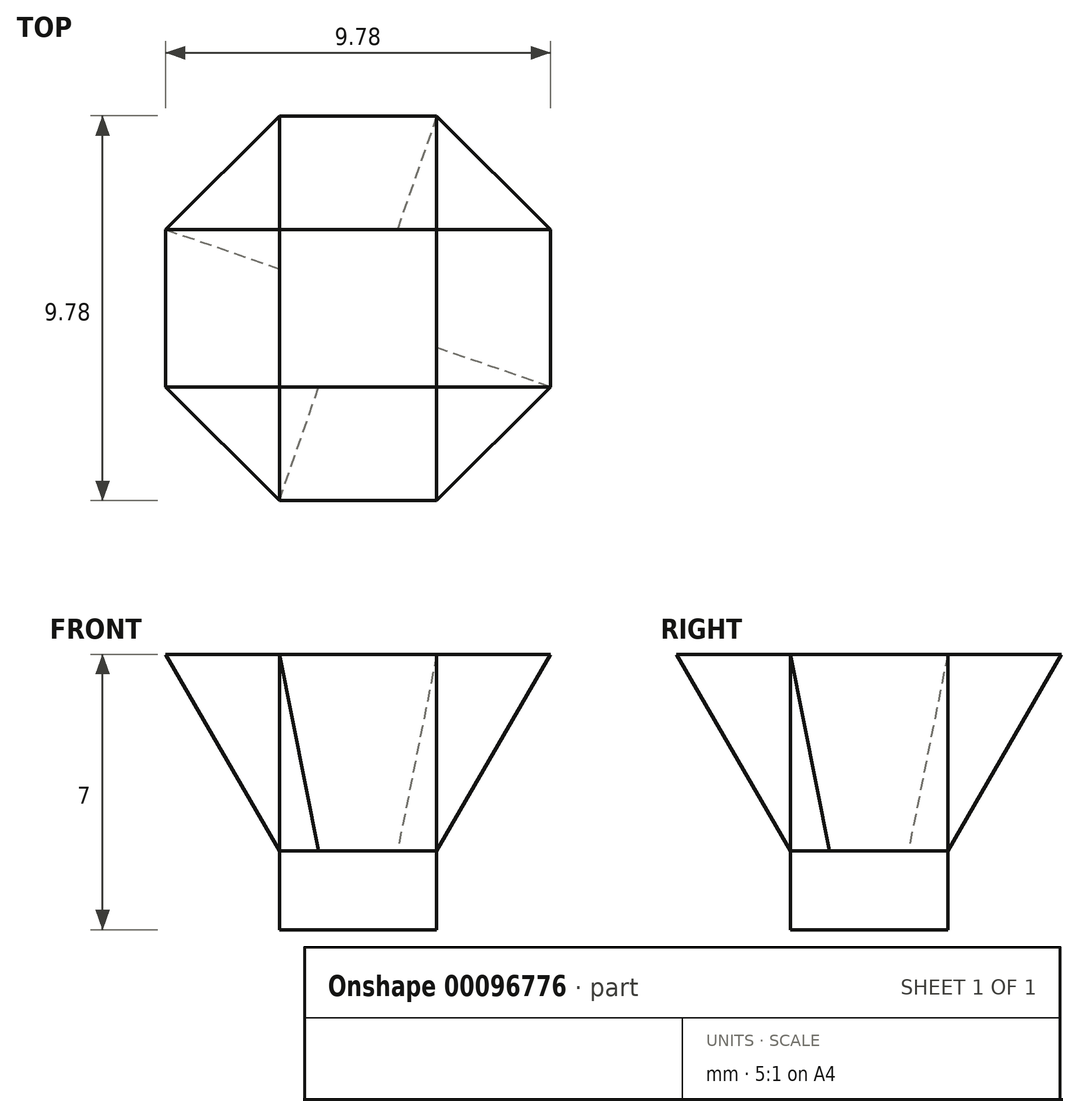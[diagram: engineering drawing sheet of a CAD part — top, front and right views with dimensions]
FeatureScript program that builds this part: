
annotation { "Feature Type Name" : "Feature", "Feature Type Description" : "" }
export const myFeature = defineFeature(function(context is Context, id is Id, definition is map)
    precondition{}
    {
        {
            var Q0;
            Q0=qCreatedBy(makeId("Front.planeOp"),FACE);
            var sketch = newSketch(context, id + "F0", { "sketchPlane" : qUnion([Q0])});
            skLineSegment(sketch, "E0.bottom", {"start": v(-2, 2.5) * mm, "end": v(2, 2.5) * mm});
            skLineSegment(sketch, "E0.top", {"start": v(-2, -2.5) * mm, "end": v(2, -2.5) * mm});
            skPoint(sketch, "E0.middle", {"position": v(0, 0) * mm});
            skLineSegment(sketch, "E1", {"start": v(-2, -2.5) * mm, "end": v(-4.89, 2.5) * mm});
            skLineSegment(sketch, "E2", {"start": v(0, 0) * mm, "end": v(0, 15.74) * mm, "construction": true});
            skLineSegment(sketch, "E3.MirrorCS", {"start": v(2, -2.5) * mm, "end": v(4.89, 2.5) * mm});
            skLineSegment(sketch, "E4", {"start": v(-2, 2.5) * mm, "end": v(-4.89, 2.5) * mm});
            skLineSegment(sketch, "E5", {"start": v(2, 2.5) * mm, "end": v(4.89, 2.5) * mm});
            skSolve(sketch);
        }
        {
            var Q0;
            Q0=qCreatedBy(makeId("Top.planeOp"),FACE);
            var sketch = newSketch(context, id + "F1", { "sketchPlane" : qUnion([Q0])});
            skPoint(sketch, "E6.0", {"position": v(-2, 0) * mm});
            skPoint(sketch, "E7.0", {"position": v(2, 0) * mm});
            skLineSegment(sketch, "E8.bottom", {"start": v(-2, -2) * mm, "end": v(2, -2) * mm});
            skLineSegment(sketch, "E8.top", {"start": v(-2, 2) * mm, "end": v(2, 2) * mm});
            skLineSegment(sketch, "E8.left", {"start": v(-2, -2) * mm, "end": v(-2, 2) * mm});
            skLineSegment(sketch, "E8.right", {"start": v(2, -2) * mm, "end": v(2, 2) * mm});
            skPoint(sketch, "E8.middle", {"position": v(0, 0) * mm});
            skSolve(sketch);
        }
        {
            var Q0;
            Q0=qCreatedBy(makeId("Top.planeOp"),FACE);
            cPlane(context, id + "F2", {"entities" : qUnion([Q0]), "cplaneType" : CPlaneType.OFFSET, "offset" : 2.5 * mm, "oppositeDirection" : true, "width" : 150 * mm, "height" : 150 * mm});
        }
        {
            var Q0;
            Q0=qCreatedBy(id+"F2.planeOp",FACE);
            var sketch = newSketch(context, id + "F3", { "sketchPlane" : qUnion([Q0])});
            skLineSegment(sketch, "E9.0.0", {"start": v(-2, 2) * mm, "end": v(-2, -2) * mm});
            skLineSegment(sketch, "E9.0.1", {"start": v(-2, -2) * mm, "end": v(2, -2) * mm});
            skLineSegment(sketch, "E9.0.2", {"start": v(2, -2) * mm, "end": v(2, 2) * mm});
            skLineSegment(sketch, "E9.0.3", {"start": v(2, 2) * mm, "end": v(-2, 2) * mm});
            skPoint(sketch, "E10", {"position": v(0, -2) * mm});
            skPoint(sketch, "E11", {"position": v(-2, 0) * mm});
            skPoint(sketch, "E12", {"position": v(0, 2) * mm});
            skPoint(sketch, "E13", {"position": v(2, 0) * mm});
            skLineSegment(sketch, "E14", {"start": v(-2, -2) * mm, "end": v(2, 2) * mm, "construction": true});
            skLineSegment(sketch, "E15", {"start": v(-2, 2) * mm, "end": v(2, -2) * mm, "construction": true});
            skLineSegment(sketch, "E16", {"start": v(0, -2) * mm, "end": v(0, 2) * mm, "construction": true});
            skLineSegment(sketch, "E17", {"start": v(-2, 0) * mm, "end": v(2, 0) * mm, "construction": true});
            skSolve(sketch);
        }
        {
            var Q0;
            Q0 = qSketchRegion(id + "F3", true);
            extrude(context, id + "F4", {"entities" : qUnion([Q0]), "oppositeDirection" : true, "depth" : 2 * mm});
        }
        {
            var Q0;
            Q0 = qSketchRegion(id + "F0", true);
            extrude(context, id + "F5", {"entities" : qUnion([Q0]), "operationType" : NewBodyOperationType.ADD, "depth" : 2 * mm, "hasSecondDirection" : true, "secondDirectionOppositeDirection" : true, "secondDirectionDepth" : 2 * mm});
        }
        {
            var Q0;
            Q0=qCreatedBy(makeId("Right.planeOp"),FACE);
            var sketch = newSketch(context, id + "F6", { "sketchPlane" : qUnion([Q0])});
            skLineSegment(sketch, "E18", {"start": v(0, -2.5) * mm, "end": v(2, -2.5) * mm});
            skLineSegment(sketch, "E19", {"start": v(0, -2.5) * mm, "end": v(-2, -2.5) * mm});
            skPoint(sketch, "E20.0", {"position": v(0, 2.5) * mm});
            skLineSegment(sketch, "E21", {"start": v(4.89, 2.5) * mm, "end": v(-4.89, 2.5) * mm});
            skLineSegment(sketch, "E22", {"start": v(2, -2.5) * mm, "end": v(4.89, 2.5) * mm});
            skLineSegment(sketch, "E23.MirrorCS", {"start": v(-2, -2.5) * mm, "end": v(-4.89, 2.5) * mm});
            skSolve(sketch);
        }
        {
            var Q0;
            Q0 = qSketchRegion(id + "F6", true);
            extrude(context, id + "F7", {"entities" : qUnion([Q0]), "depth" : 2 * mm, "hasSecondDirection" : true, "secondDirectionOppositeDirection" : true, "secondDirectionDepth" : 2 * mm});
        }
        {
            var Q0;
            Q0=qCreatedBy(makeId("Top.planeOp"),FACE);
            cPlane(context, id + "F8", {"entities" : qUnion([Q0]), "cplaneType" : CPlaneType.OFFSET, "offset" : 2.5 * mm, "width" : 150 * mm, "height" : 150 * mm});
        }
        {
            var Q0;
            Q0=qCreatedBy(id+"F8.planeOp",FACE);
            var sketch = newSketch(context, id + "F9", { "sketchPlane" : qUnion([Q0])});
            skLineSegment(sketch, "E24.0", {"start": v(2, 4.89) * mm, "end": v(-2, 4.89) * mm});
            skLineSegment(sketch, "E25.0", {"start": v(-4.89, -2) * mm, "end": v(-4.89, 2) * mm});
            skLineSegment(sketch, "E26.0", {"start": v(2, -4.89) * mm, "end": v(-2, -4.89) * mm});
            skLineSegment(sketch, "E27.0", {"start": v(4.89, -2) * mm, "end": v(4.89, 2) * mm});
            skLineSegment(sketch, "E28", {"start": v(-4.89, 2) * mm, "end": v(-2, 4.89) * mm});
            skLineSegment(sketch, "E29", {"start": v(2, 4.89) * mm, "end": v(4.89, 2) * mm});
            skLineSegment(sketch, "E30", {"start": v(4.89, -2) * mm, "end": v(2, -4.89) * mm});
            skLineSegment(sketch, "E31", {"start": v(-2, -4.89) * mm, "end": v(-4.89, -2) * mm});
            skLineSegment(sketch, "E32", {"start": v(-2, 4.89) * mm, "end": v(2, -4.89) * mm, "construction": true});
            skLineSegment(sketch, "E33", {"start": v(-2, -4.89) * mm, "end": v(2, 4.89) * mm, "construction": true});
            skLineSegment(sketch, "E34", {"start": v(-4.89, 2) * mm, "end": v(4.89, -2) * mm, "construction": true});
            skLineSegment(sketch, "E35", {"start": v(-4.89, -2) * mm, "end": v(4.89, 2) * mm, "construction": true});
            skPoint(sketch, "E36", {"position": v(3.44, 3.44) * mm});
            skPoint(sketch, "E37", {"position": v(0, 4.89) * mm});
            skPoint(sketch, "E38", {"position": v(-3.44, 3.44) * mm});
            skPoint(sketch, "E39", {"position": v(-4.89, 0) * mm});
            skPoint(sketch, "E40", {"position": v(-3.44, -3.44) * mm});
            skPoint(sketch, "E41", {"position": v(0, -4.89) * mm});
            skPoint(sketch, "E42", {"position": v(3.44, -3.44) * mm});
            skPoint(sketch, "E43", {"position": v(4.89, 0) * mm});
            skLineSegment(sketch, "E44", {"start": v(-3.44, 3.44) * mm, "end": v(3.44, -3.44) * mm, "construction": true});
            skLineSegment(sketch, "E45", {"start": v(0, 4.89) * mm, "end": v(0, -4.89) * mm, "construction": true});
            skLineSegment(sketch, "E46", {"start": v(-3.44, -3.44) * mm, "end": v(3.44, 3.44) * mm, "construction": true});
            skLineSegment(sketch, "E47", {"start": v(-4.89, 0) * mm, "end": v(4.89, 0) * mm, "construction": true});
            skSolve(sketch);
        }
        {
            var Q0;
            Q0=makeQuery(id+"F9.imprint","IMPRINT",FACE,{"disambiguationData":[TD([[makeQuery(id+"F9.imprint","IMPRINT",EDGE,{"derivedFrom":sQuery(id+"F9.wireOp",EDGE,"E24.0")}),1.0]])]});
            var Q1;
            Q1=makeQuery(id+"F3.imprint","IMPRINT",FACE,{"disambiguationData":[TD([[makeQuery(id+"F3.imprint","IMPRINT",EDGE,{"derivedFrom":sQuery(id+"F3.wireOp",EDGE,"E9.0.0")}),1.0]])]});
            var Q2;
            Q2=sQuery(id+"F0.wireOp",EDGE,"E1");
            var Q3;
            Q3=sQuery(id+"F6.wireOp",EDGE,"E23.MirrorCS");
            var Q4;
            Q4=sQuery(id+"F0.wireOp",EDGE,"E3.MirrorCS");
            var Q5;
            Q5=sQuery(id+"F6.wireOp",EDGE,"E22");
            var Q6;
            Q6=sQuery(id+"F3.wireOp",VERTEX,"E15.end");
            var Q7;
            Q7=sQuery(id+"F9.wireOp",VERTEX,"E34.end");
            var Q8;
            Q8=sQuery(id+"F3.wireOp",VERTEX,"E14.start");
            var Q9;
            Q9=sQuery(id+"F9.wireOp",VERTEX,"E40");
            var Q10;
            Q10=sQuery(id+"F9.wireOp",VERTEX,"E42");
            var Q11;
            Q11=sQuery(id+"F9.wireOp",VERTEX,"E27.0.start");
            var Q12;
            Q12=sQuery(id+"F9.wireOp",VERTEX,"E32.end");
            var Q13;
            Q13=sQuery(id+"F9.wireOp",VERTEX,"E26.0.end");
            var Q14;
            Q14=sQuery(id+"F9.wireOp",VERTEX,"E35.start");
            var Q15;
            Q15=sQuery(id+"F9.wireOp",VERTEX,"E39");
            var Q16;
            Q16=sQuery(id+"F9.wireOp",VERTEX,"E32.start");
            var Q17;
            Q17=sQuery(id+"F9.wireOp",VERTEX,"E36");
            var Q18;
            Q18=sQuery(id+"F9.wireOp",VERTEX,"E24.0.start");
            var Q19;
            Q19=sQuery(id+"F9.wireOp",VERTEX,"E41");
            var Q20;
            Q20=sQuery(id+"F9.wireOp",VERTEX,"E37");
            var Q21;
            Q21=sQuery(id+"F9.wireOp",VERTEX,"E35.end");
            var Q22;
            Q22=sQuery(id+"F3.wireOp",VERTEX,"E10");
            loft(context, id + "F10", {"addGuides" : true, "sheetProfilesArray" : [{ "sheetProfileEntities" : qUnion([Q0]) }, { "sheetProfileEntities" : qUnion([Q1]) }], "guidesArray" : [{ "guideEntities" : qUnion([Q2]), "guideDerivativeType" : LoftGuideDerivativeType.DEFAULT, "guideDerivativeMagnitude" : 1 }, { "guideEntities" : qUnion([Q3]), "guideDerivativeType" : LoftGuideDerivativeType.DEFAULT, "guideDerivativeMagnitude" : 1 }, { "guideEntities" : qUnion([Q4]), "guideDerivativeType" : LoftGuideDerivativeType.DEFAULT, "guideDerivativeMagnitude" : 1 }, { "guideEntities" : qUnion([Q5]), "guideDerivativeType" : LoftGuideDerivativeType.DEFAULT, "guideDerivativeMagnitude" : 1 }], "connections" : [{ "connectionEntities" : qUnion([Q6, Q7, Q8, Q9, Q10, Q11, Q12, Q13, Q14, Q15, Q16, Q17, Q18, Q19, Q20, Q21, Q22]), "connectionEdgeQueries" : qUnion([]), "connectionEdgeParameters" : [] }]});
        }
    });
